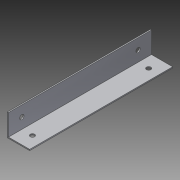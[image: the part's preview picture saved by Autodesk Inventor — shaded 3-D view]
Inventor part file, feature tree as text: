
AUTODESK INVENTOR PART (.ipt)
format: ipt  version: 2014 SP1 (Build 180222100, 222)  size: 100,864 bytes
history: native  units: in
note: dims shown in document units (in); Inventor stores cm internally (conversion verified against a paired STEP export)
features: extrude x3, sketch x3
ambient origin geometry x8: Origin, YZ Plane, XZ Plane, XY Plane, X Axis, Y Axis, Z Axis, Center Point
bodies: Solid1 (feature_tree)
feature tree (6):
  extrude  "Extrusion1"  Depth=0.0312in
  sketch  "Sketch2"  dims[d2=4.0in d3=0.0in d4=0.375in]
  sketch  "Sketch3"  dims[d5=0.125in d6=4.0in d7=0.7874in d9=3.25in d10=0.3937in d12=1.0in d14=0.125in d15=0.375in d16=4.0in d17=0.7874in d19=3.25in d20=0.3937in d22=1.0in d24=1.0in d25=0.0in d26=1.0in d27=0.0in]
  extrude  "Extrusion2"  Depth=4.0in
  extrude  "Extrusion3"  Depth=4.0in
  sketch  "Sketch1"  dims[d0=0.625in d1=0.0312in]
